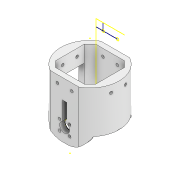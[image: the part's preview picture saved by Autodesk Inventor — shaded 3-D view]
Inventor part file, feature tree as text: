
AUTODESK INVENTOR PART (.ipt)
format: ipt  version: 2021 (Build 250183000, 183)  size: 474,624 bytes
history: native  units: mm
features: sketch x27, extrude x22, chamfer x1
ambient origin geometry x8: Origin, YZ Plane, XZ Plane, XY Plane, X Axis, Y Axis, Z Axis, Center Point
bodies: Body1 (feature_tree)
feature tree (50):
  extrude  "Extrusión2"  Depth=100.0mm TaperAngle=0.0deg
  sketch  "Boceto5"  dims[d45=100.0mm d46=0.0mm d53=10.0mm]
  sketch  "Boceto7"  dims[d54=10.0mm d55=25.0mm]
  extrude  "Extrusión4"  Depth=10.0mm
  extrude  "Extrusión8"  Depth=25.0mm
  extrude  "Extrusión12"  Depth=20.0mm
  extrude  "Extrusión13"  Depth=30.0mm
  sketch  "Boceto14"  dims[d62=200.0mm d63=0.0mm d95=8.0mm]
  extrude  "Extrusión16"  Depth=8.0mm
  extrude  "Extrusión17"  Depth=3.0mm
  extrude  "Extrusión18"  Depth=8.0mm
  extrude  "Extrusión19"  Depth=200.0mm TaperAngle=0.0deg
  extrude  "Extrusión20"  Depth=1000.0mm TaperAngle=0.0deg
  extrude  "Extrusión21"  Depth=1000.0mm TaperAngle=0.0deg
  sketch  "Boceto22"  dims[d151=20.0mm d152=5.0mm d153=1000.0mm d154=0.0mm]
  extrude  "Extrusión22"  Depth=1000.0mm TaperAngle=0.0deg
  extrude  "Extrusión23"  Depth=20.0mm
  chamfer  "Chaflán3"  Distance=1000.0mm
  sketch  "Boceto25"  dims[d167=2.0mm d168=2.0mm d169=45.0deg d170=25.0mm d171=0.0mm]
  extrude  "Extrusión24"  Depth=20.0mm TaperAngle=0.0deg
  sketch  "Boceto27"  dims[d179=250.0mm d180=0.0mm d181=15.0mm]
  extrude  "Extrusión25"  Depth=20.0mm TaperAngle=0.0deg
  extrude  "Extrusión26"  Depth=25.0mm TaperAngle=0.0deg
  sketch  "Boceto30"  dims[d189=5.0mm d190=5.0mm]
  extrude  "Extrusión27"  Depth=3.0mm
  extrude  "Extrusión28"  Depth=15.0mm
  extrude  "Extrusión29"  Depth=1010.0mm TaperAngle=0.0deg
  sketch  "Boceto34"  dims[d12=0.872665mm]
  extrude  "Extrusión30"  Depth=5.0mm TaperAngle=0.0deg
  extrude  "Extrusión31"  Depth=5.0mm
  extrude  "Extrusión32"  Depth=200.0mm TaperAngle=0.0deg
  sketch  "Boceto4"  dims[d20=40.0mm d22=360.0deg d28=100.0mm d29=0.0mm]
  sketch  "Boceto10"  dims[d58=20.0mm d59=20.0mm]
  sketch  "Boceto11"  dims[d60=30.0mm d61=30.0mm]
  sketch  "Boceto15"  dims[d96=8.0mm d97=3.0mm]
  sketch  "Boceto16"  dims[d98=8.0mm d99=8.0mm]
  sketch  "Boceto17"  dims[d100=3.0mm d101=200.0mm d102=0.0mm]
  sketch  "Boceto18"  dims[d111=200.0mm d112=0.0mm d126=1000.0mm d127=0.0mm]
  sketch  "Boceto19"  dims[d128=1000.0mm d129=0.0mm d130=1000.0mm d131=0.0mm]
  sketch  "Boceto21"  dims[d132=1000.0mm d133=0.0mm d134=1000.0mm d135=0.0mm]
  sketch  "Boceto23"  dims[d155=8.0mm d156=20.0mm d157=0.0mm]
  sketch  "Boceto24"  dims[d164=8.0mm d165=20.0mm d166=0.0mm]
  sketch  "Boceto26"  dims[d172=250.0mm d173=0.0mm d178=3.0mm]
  sketch  "Boceto28"  dims[d182=15.0mm d183=1010.0mm d184=0.0mm]
  sketch  "Boceto29"  dims[d185=5.0mm d186=0.0mm d187=5.0mm d188=0.0mm]
  sketch  "Boceto31"  dims[d193=200.0mm d194=0.0mm d195=200.0mm d196=0.0mm]
  sketch  "Boceto32"  dims[d197=20.0mm d198=0.0mm]
  sketch  "Boceto33"  dims[d11=0.5mm]
  sketch  "Boceto35"  dims[d13=0.5mm]
  sketch  "Boceto36"  dims[d14=0.872665mm d30=0.5mm d31=0.872665mm d36=0.5mm d37=0.872665mm d38=0.5mm d39=0.872665mm d47=0.5mm d48=0.872665mm d49=0.5mm d50=0.872665mm d68=0.5mm d69=0.872665mm d70=0.5mm d71=0.872665mm d191=0.5mm d192=0.872665mm]
